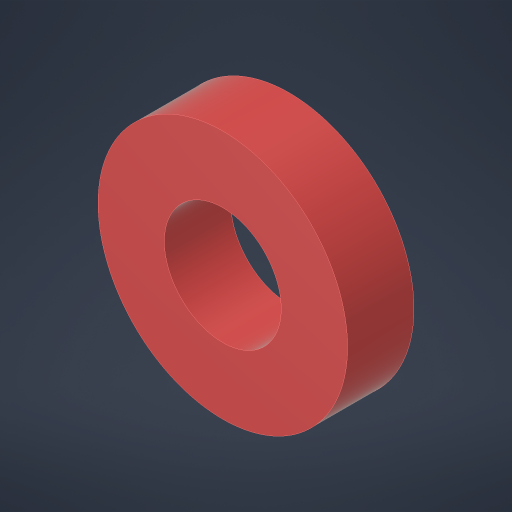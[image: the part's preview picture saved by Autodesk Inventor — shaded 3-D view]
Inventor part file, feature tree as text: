
AUTODESK INVENTOR PART (.ipt)
format: ipt  version: 2023.4 (Build 274418000, 418)  size: 168,448 bytes
history: native  units: in
note: dims shown in document units (in); Inventor stores cm internally (conversion verified against a paired STEP export)
features: extrude x1, sketch x1
ambient origin geometry x8: Origin, YZ Plane, XZ Plane, XY Plane, X Axis, Y Axis, Z Axis, Center Point
bodies: Solid1 (feature_tree)
feature tree (2):
  extrude  "Extrusion1"  Depth=0.5in TaperAngle=0.0deg
  sketch  "Sketch1"  dims[d0=0.5in d1=0.5in d2=0.0in d3=0.88in]
